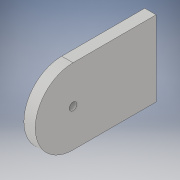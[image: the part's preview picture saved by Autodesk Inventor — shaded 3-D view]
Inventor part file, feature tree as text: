
AUTODESK INVENTOR PART (.ipt)
format: ipt  version: 2019 (Build 230136000, 136)  size: 106,496 bytes
history: native  units: mm
features: sketch x2, other x1, extrude x1, hole x1
ambient origin geometry x8: Origin, YZ Plane, XZ Plane, XY Plane, X Axis, Y Axis, Z Axis, Center Point
bodies: Body1 (feature_tree)
feature tree (5):
  other  "ソリッド1"
  extrude  "押し出し1"  Depth=20.0mm
  hole  "穴1"  [1 undecoded]
  sketch  "スケッチ1"
  sketch  "スケッチ2"
note: 1 required parameter value undecoded (feature->parameter linkage not recoverable at this tier; creation-order binding heuristic only, values carry confidence <= 0.55)
